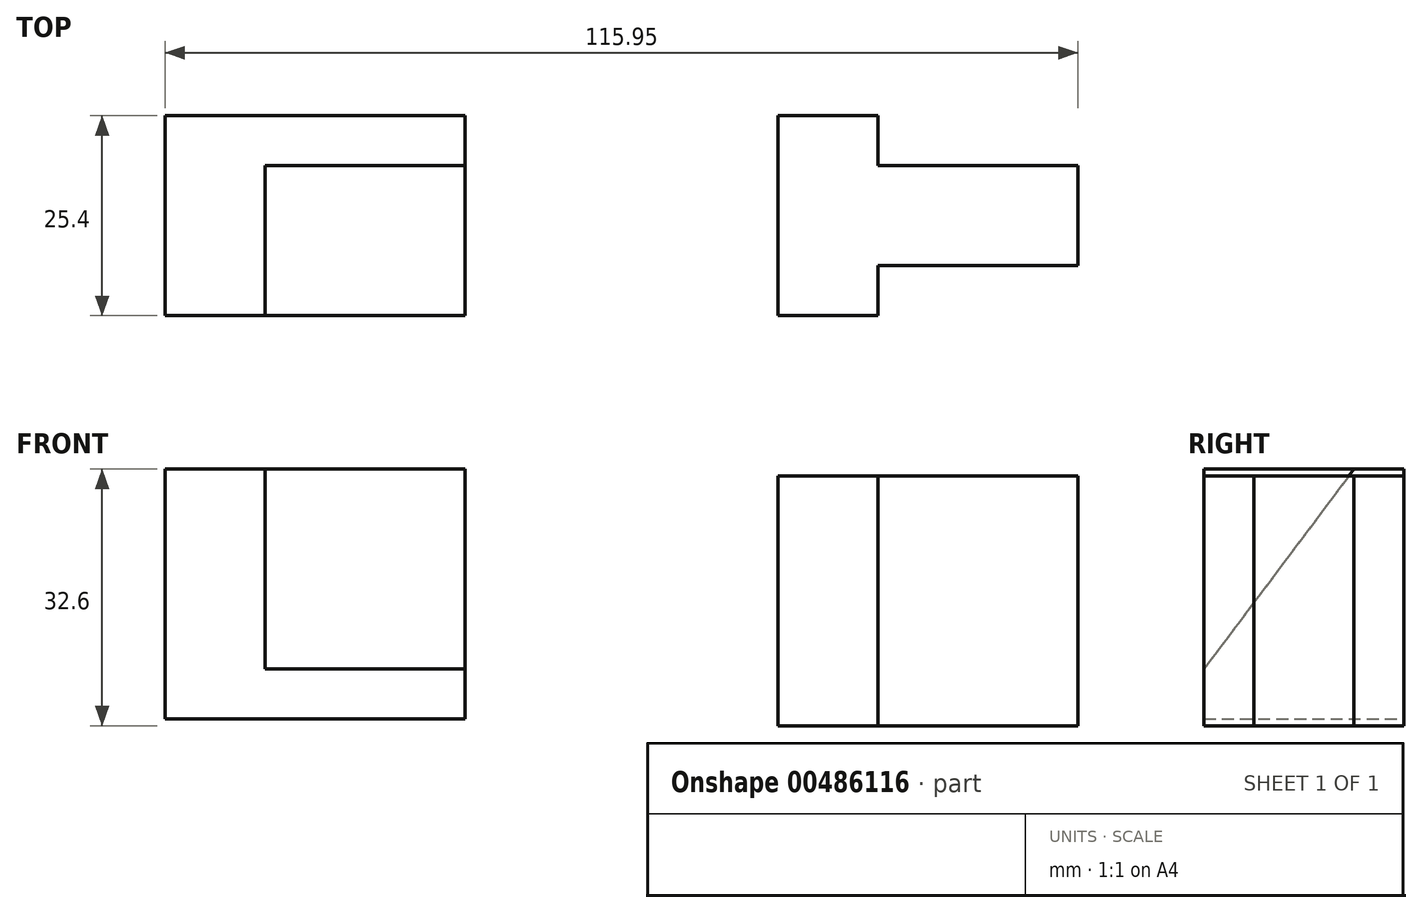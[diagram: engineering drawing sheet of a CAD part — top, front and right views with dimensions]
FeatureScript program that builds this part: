
annotation { "Feature Type Name" : "Feature", "Feature Type Description" : "" }
export const myFeature = defineFeature(function(context is Context, id is Id, definition is map)
    precondition{}
    {
        {
            var Q0;
            Q0=qCreatedBy(makeId("Front.planeOp"),FACE);
            var sketch = newSketch(context, id + "F0", { "sketchPlane" : qUnion([Q0])});
            skLineSegment(sketch, "E0", {"start": v(-64.39, 3.13) * mm, "end": v(-26.29, 3.13) * mm});
            skLineSegment(sketch, "E1", {"start": v(-26.29, 3.13) * mm, "end": v(-26.29, 34.88) * mm});
            skLineSegment(sketch, "E2", {"start": v(-26.29, 34.88) * mm, "end": v(-64.39, 34.88) * mm});
            skLineSegment(sketch, "E3", {"start": v(-64.39, 34.88) * mm, "end": v(-64.39, 3.13) * mm});
            skSolve(sketch);
        }
        {
            var Q0;
            Q0=makeQuery(id+"F0.imprint","IMPRINT",FACE,{"disambiguationData":[TD([[makeQuery(id+"F0.imprint","IMPRINT",EDGE,{"derivedFrom":sQuery(id+"F0.wireOp",EDGE,"E0")}),1.0]])]});
            extrude(context, id + "F1", {"entities" : qUnion([Q0]), "depth" : 25.4 * mm, "offsetDistance" : 25.4 * mm});
        }
        {
            var Q0;
            Q0=makeQuery(id+"F1.opExtrude","SWEPT_FACE",FACE,{"disambiguationData":[OSD([sQuery(id+"F0.wireOp",EDGE,"E1")])]});
            var sketch = newSketch(context, id + "F2", { "sketchPlane" : qUnion([Q0])});
            skLineSegment(sketch, "E4", {"start": v(-6.35, 34.88) * mm, "end": v(-25.4, 9.48) * mm});
            skSolve(sketch);
        }
        {
            var Q0;
            {var subQ0=sQuery(id+"F2.wireOp",EDGE,"E4");Q0=makeQuery(id+"F2.imprint","IMPRINT",FACE,{"disambiguationData":[TD([[makeQuery(id+"F2.imprint","IMPRINT",EDGE,{"derivedFrom":subQ0}),-1.0]])]});}
            extrude(context, id + "F3", {"entities" : qUnion([Q0]), "operationType" : NewBodyOperationType.REMOVE, "oppositeDirection" : true, "depth" : 25.4 * mm, "offsetDistance" : 25.4 * mm});
        }
        {
            var Q0;
            Q0=qCreatedBy(makeId("Front.planeOp"),FACE);
            var sketch = newSketch(context, id + "F4", { "sketchPlane" : qUnion([Q0])});
            skLineSegment(sketch, "E5", {"start": v(13.46, 34.03) * mm, "end": v(13.46, 2.28) * mm});
            skLineSegment(sketch, "E6", {"start": v(13.46, 2.28) * mm, "end": v(51.56, 2.28) * mm});
            skLineSegment(sketch, "E7", {"start": v(51.56, 2.28) * mm, "end": v(51.56, 34.03) * mm});
            skLineSegment(sketch, "E8", {"start": v(51.56, 34.03) * mm, "end": v(13.46, 34.03) * mm});
            skSolve(sketch);
        }
        {
            var Q0;
            Q0=makeQuery(id+"F4.imprint","IMPRINT",FACE,{"disambiguationData":[TD([[makeQuery(id+"F4.imprint","IMPRINT",EDGE,{"derivedFrom":sQuery(id+"F4.wireOp",EDGE,"E5")}),1.0]])]});
            extrude(context, id + "F5", {"entities" : qUnion([Q0]), "depth" : 25.4 * mm, "offsetDistance" : 25.4 * mm});
        }
        {
            var Q0;
            Q0=makeQuery(id+"F5.opExtrude","CAP_FACE",FACE,{"disambiguationData":[OSD([sQuery(id+"F4.wireOp",EDGE,"E5"),sQuery(id+"F4.wireOp",EDGE,"E6"),sQuery(id+"F4.wireOp",EDGE,"E7"),sQuery(id+"F4.wireOp",EDGE,"E8")])],"isStart":false});
            var sketch = newSketch(context, id + "F6", { "sketchPlane" : qUnion([Q0])});
            skLineSegment(sketch, "E9", {"start": v(26.16, 34.03) * mm, "end": v(26.16, 2.28) * mm});
            skSolve(sketch);
        }
        {
            var Q0;
            {var subQ0=sQuery(id+"F6.wireOp",EDGE,"E9");Q0=makeQuery(id+"F6.imprint","IMPRINT",FACE,{"disambiguationData":[TD([[makeQuery(id+"F6.imprint","IMPRINT",EDGE,{"derivedFrom":subQ0}),1.0]])]});}
            extrude(context, id + "F7", {"entities" : qUnion([Q0]), "operationType" : NewBodyOperationType.REMOVE, "oppositeDirection" : true, "depth" : 6.35 * mm, "offsetDistance" : 25.4 * mm});
        }
        {
            var Q0;
            Q0=makeQuery(id+"F5.opExtrude","CAP_FACE",FACE,{"disambiguationData":[OSD([sQuery(id+"F4.wireOp",EDGE,"E5"),sQuery(id+"F4.wireOp",EDGE,"E6"),sQuery(id+"F4.wireOp",EDGE,"E7"),sQuery(id+"F4.wireOp",EDGE,"E8")])],"isStart":true});
            var sketch = newSketch(context, id + "F8", { "sketchPlane" : qUnion([Q0])});
            skLineSegment(sketch, "E10", {"start": v(-26.16, 34.03) * mm, "end": v(-26.16, 2.28) * mm});
            skSolve(sketch);
        }
        {
            var Q0;
            {var subQ0=sQuery(id+"F8.wireOp",EDGE,"E10");Q0=makeQuery(id+"F8.imprint","IMPRINT",FACE,{"disambiguationData":[TD([[makeQuery(id+"F8.imprint","IMPRINT",EDGE,{"derivedFrom":subQ0}),-1.0]])]});}
            extrude(context, id + "F9", {"entities" : qUnion([Q0]), "operationType" : NewBodyOperationType.REMOVE, "oppositeDirection" : true, "depth" : 6.35 * mm, "offsetDistance" : 25.4 * mm});
        }
    });
